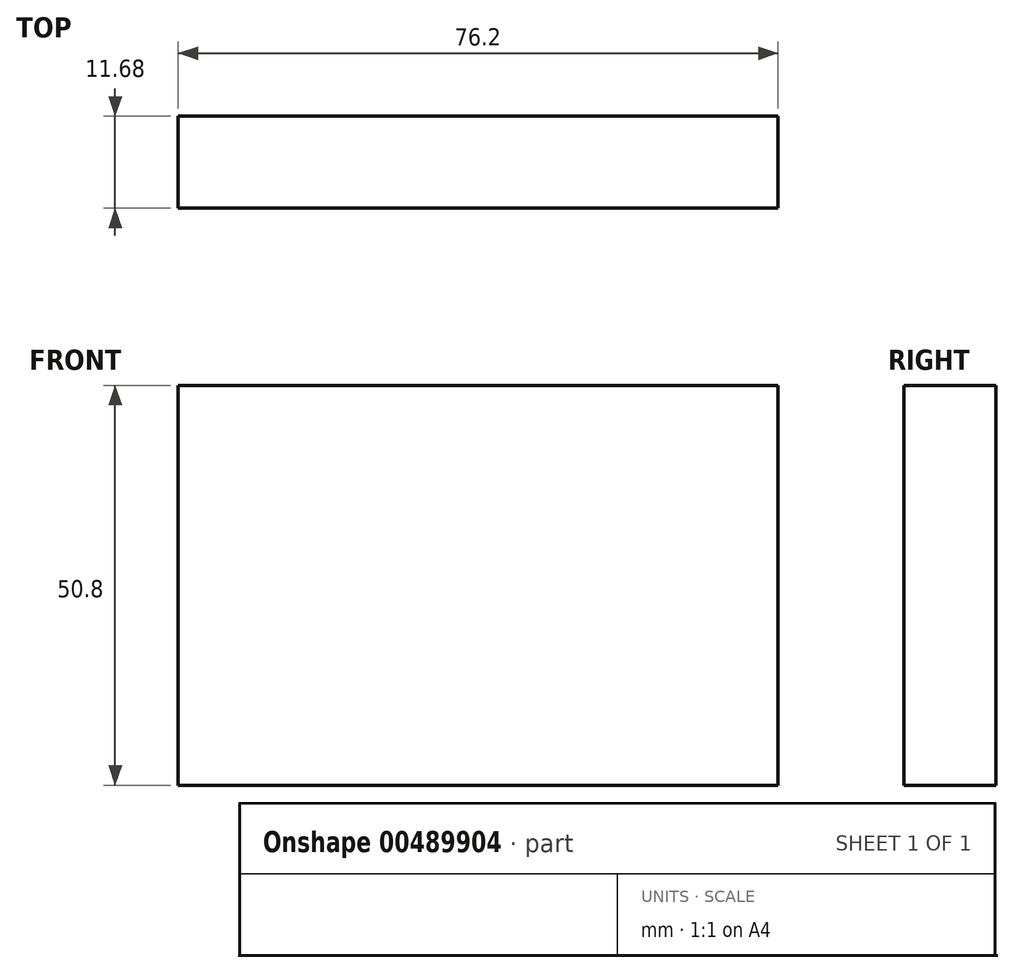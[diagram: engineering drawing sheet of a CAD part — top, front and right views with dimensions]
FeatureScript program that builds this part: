
annotation { "Feature Type Name" : "Feature", "Feature Type Description" : "" }
export const myFeature = defineFeature(function(context is Context, id is Id, definition is map)
    precondition{}
    {
        {
            var Q0;
            Q0=qCreatedBy(makeId("Front.planeOp"),FACE);
            var sketch = newSketch(context, id + "F0", { "sketchPlane" : qUnion([Q0])});
            skLineSegment(sketch, "E0", {"start": v(-23.6, 26.94) * mm, "end": v(-23.6, -23.86) * mm});
            skLineSegment(sketch, "E1", {"start": v(-23.6, -23.86) * mm, "end": v(52.6, -23.86) * mm});
            skLineSegment(sketch, "E2", {"start": v(-23.6, 26.94) * mm, "end": v(52.6, 26.94) * mm});
            skLineSegment(sketch, "E3", {"start": v(52.6, 26.94) * mm, "end": v(52.6, -23.86) * mm});
            skSolve(sketch);
        }
        {
            var Q0;
            Q0 = qSketchRegion(id + "F0", true);
            extrude(context, id + "F1", {"entities" : qUnion([Q0]), "depth" : 5.84 * mm});
        }
        {
            var Q0;
            Q0=makeQuery(id+"F1.opExtrude","SWEPT_BODY",BODY,{"disambiguationData":[OSD([sQuery(id+"F0.wireOp",EDGE,"E0"),sQuery(id+"F0.wireOp",EDGE,"E1"),sQuery(id+"F0.wireOp",EDGE,"E2"),sQuery(id+"F0.wireOp",EDGE,"E3")])]});
            var Q1;
            Q1=makeQuery(id+"F1.opExtrude","CAP_FACE",FACE,{"disambiguationData":[OSD([sQuery(id+"F0.wireOp",EDGE,"E0"),sQuery(id+"F0.wireOp",EDGE,"E1"),sQuery(id+"F0.wireOp",EDGE,"E2"),sQuery(id+"F0.wireOp",EDGE,"E3")])],"isStart":true});
            mirror(context, id + "F2", {"operationType" : NewBodyOperationType.ADD, "entities" : qUnion([Q0]), "mirrorPlane" : qUnion([Q1])});
        }
    });
